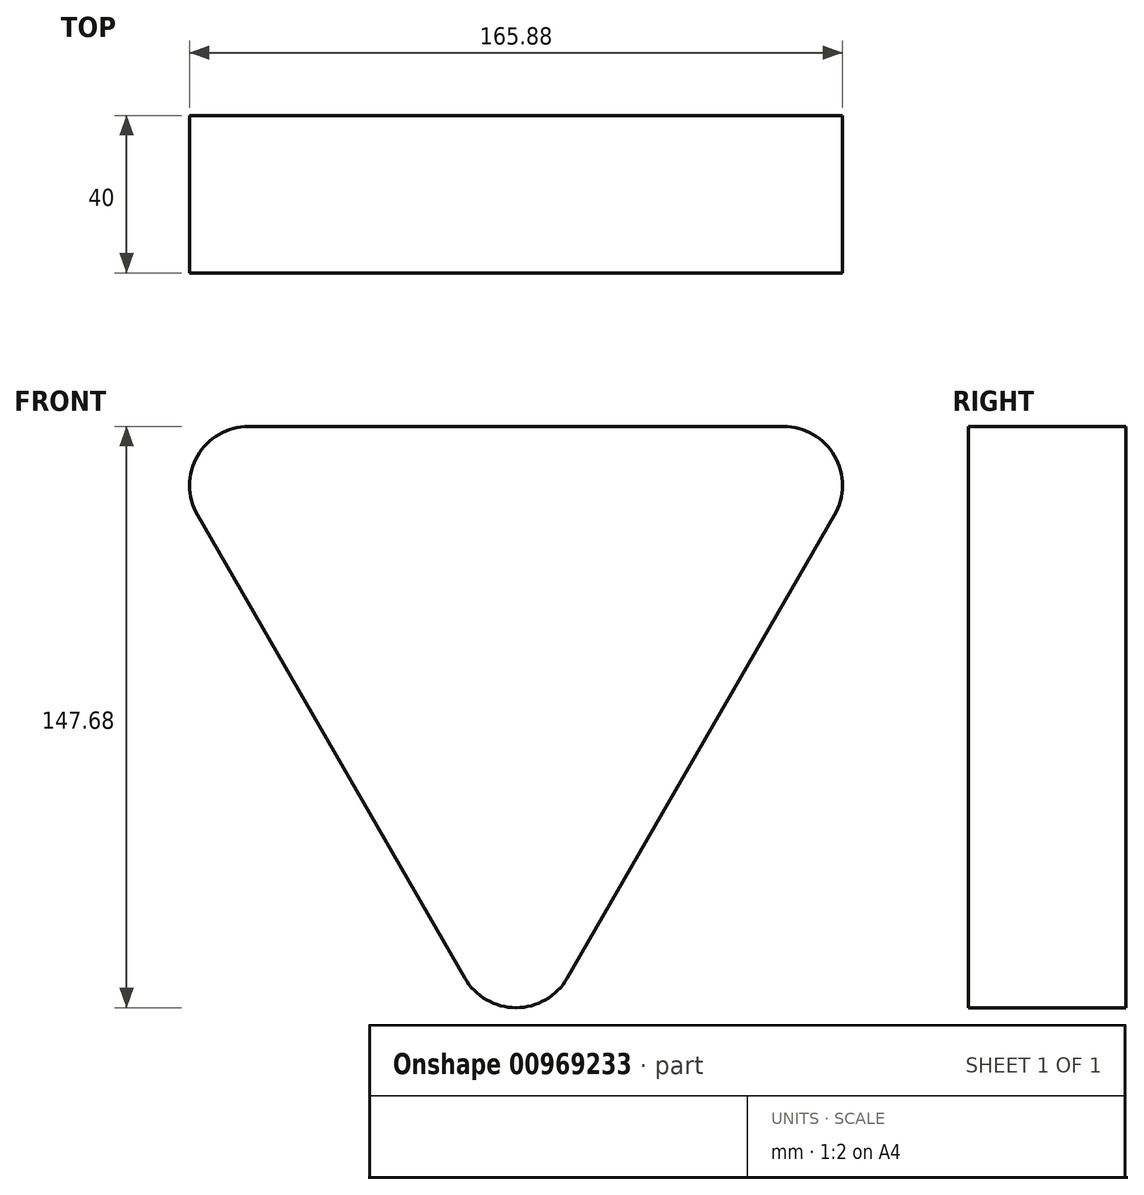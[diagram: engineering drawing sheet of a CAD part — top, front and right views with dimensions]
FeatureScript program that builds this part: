
annotation { "Feature Type Name" : "Feature", "Feature Type Description" : "" }
export const myFeature = defineFeature(function(context is Context, id is Id, definition is map)
    precondition{}
    {
        {
            var Q0;
            Q0=qCreatedBy(makeId("Front.planeOp"),FACE);
            var sketch = newSketch(context, id + "F0", { "sketchPlane" : qUnion([Q0])});
            skCircle(sketch, "E0.cCircle", {"center": v(0, 0) * mm, "radius": 54.23 * mm, "construction": true});
            skLineSegment(sketch, "E0.0", {"start": v(-67.94, 54.23) * mm, "end": v(67.94, 54.23) * mm});
            skLineSegment(sketch, "E0.1", {"start": v(80.93, 31.73) * mm, "end": v(13, -85.95) * mm});
            skLineSegment(sketch, "E0.2", {"start": v(-13, -85.95) * mm, "end": v(-80.93, 31.73) * mm});
            skPoint(sketch, "E0.0.midPoint", {"position": v(0, 54.23) * mm});
            skPoint(sketch, "E1.visualSharp", {"position": v(-93.92, 54.23) * mm});
            skArc(sketch, "E1.filletArc", {"start": v(-67.94, 54.23) * mm, "mid": v(-80.93, 46.73) * mm, "end": v(-80.93, 31.73) * mm});
            skPoint(sketch, "E2.visualSharp", {"position": v(93.92, 54.23) * mm});
            skArc(sketch, "E2.filletArc", {"start": v(80.93, 31.73) * mm, "mid": v(80.93, 46.73) * mm, "end": v(67.94, 54.23) * mm});
            skPoint(sketch, "E3.visualSharp", {"position": v(0, -108.45) * mm});
            skArc(sketch, "E3.filletArc", {"start": v(-13, -85.95) * mm, "mid": v(0, -93.45) * mm, "end": v(13, -85.95) * mm});
            skSolve(sketch);
        }
        {
            var Q0;
            Q0=makeQuery(id+"F0.imprint","IMPRINT",FACE,{"disambiguationData":[TD([[makeQuery(id+"F0.imprint","IMPRINT",EDGE,{"derivedFrom":sQuery(id+"F0.wireOp",EDGE,"E0.0")}),-1.0]])]});
            extrude(context, id + "F1", {"entities" : qUnion([Q0]), "oppositeDirection" : true, "depth" : 40 * mm, "offsetDistance" : 25 * mm});
        }
    });
